# Revit family: RN 82018 Optipress-Aquaplus-Set de montage
name_source: partatom
category: Rohrzubehör
units: mm (PartAtom-declared; Revit-internal decimal feet)

## family parameters
Arbeitsebenenbasiert = Nein
Beim Laden mit Abzugskörper schneiden = Nein
Bemaßung runder Anschluss = Durchmesser verwenden
Gemeinsam genutzt = Nein
Immer vertikal = Ja
Teiletyp = Ventil - Zerlegung in

## types (1)
- DN 20
    1.010.00.2 Numéro de feuille de la directive = 17
    1.010.00.3 Date de publication (mois) de la ligne directrice = 201601
    1.010.00.4 Nom du Fabricant = R. Nussbaum AG
    1.010.00.5 Date de révision du fichier = 20190528
    1.010.00.6 Adresse Web du fabricant = http://www.nussbaum.ch
    1.100.00.3 Numéro de tri pour la séquence d'affichage = 7
    1.100.00.4 Désignation du produit = Dispositifs de mesure et de comptage
    1.800.00.3 Numéro BS = 0070120000000000000000000000020070000000000000000100000000
    1.810.00.3 Numéro de commande fabricant = 82018.24
    1.810.00.4 Numéro DATANORM = 82018.24
    1.810.00.5 Numéro StLB = 652.825
    1.810.00.6 Numéro GTIN = 7612945656513
    1.960/3L.00.8 Lien (URL) = https://www.nussbaum.ch
    17.700.00.30 Description du produit = 82018.24, Optipress-Aquaplus-Set de montage, pour compteur à capsule Koax, DN=20
    17.700.00.4 Type d'assemblage de soupape = 9
    17.700.00.5 DN de taille nominale = 20
    17.700.00.6 Kvs-value [m3/h] = 4.15
    17.700.00.7 Température de fonctionnement maximale TB [°C] = 90
    17.700.00.8 Pression de service maximale (pression de service) ps [1.0 · 105 Pa] = 10
    CONNECTOR0_DIAMETER_dX_0r = 20 mm
    CONNECTOR0_dX_00 = 68 mm
    CONNECTOR0_dX_01 = 45 mm
    CONNECTOR0_ref_dX = 45 mm
    CONNECTOR1_DIAMETER_dX_0r = 20 mm
    CONNECTOR1_dX_00 = 45 mm
    CONNECTOR1_dX_01 = 68 mm
    CONNECTOR1_ref_dX = 45 mm
    Connector Visibility = Nein
    EnclosingSpace Visibility = Nein
    R. Nussbaum AG 82018.24 fr Visibility = Ja

## geometry (parser evidence)
native form markers: Sweep x3
no freeform markers — native parametric forms only
